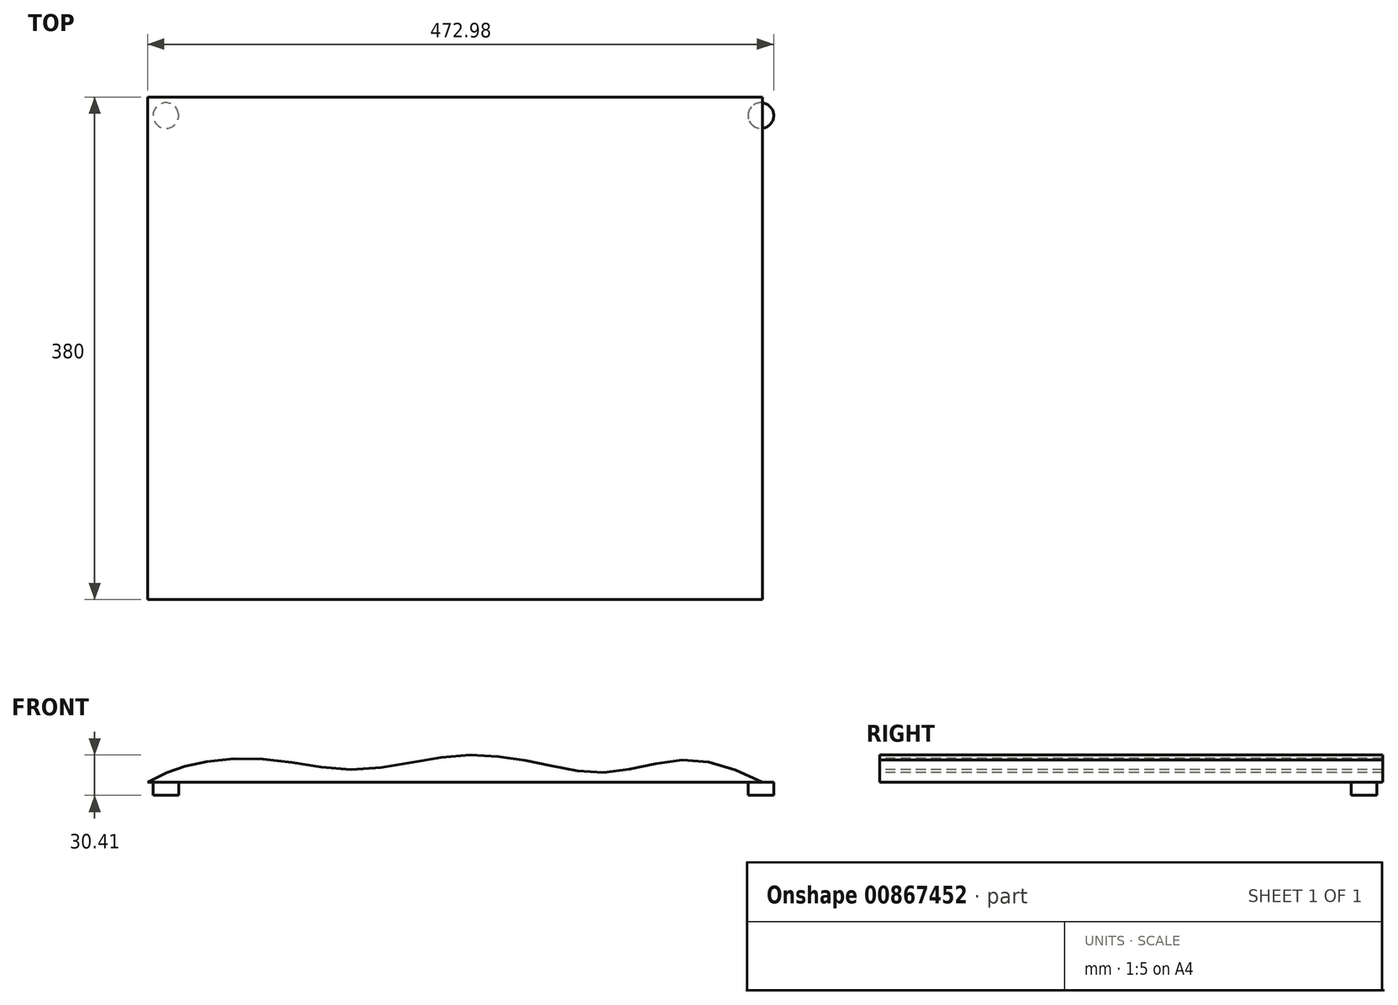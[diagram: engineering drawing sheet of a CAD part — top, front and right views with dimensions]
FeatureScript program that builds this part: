
annotation { "Feature Type Name" : "Feature", "Feature Type Description" : "" }
export const myFeature = defineFeature(function(context is Context, id is Id, definition is map)
    precondition{}
    {
        {
            var Q0;
            Q0=qCreatedBy(makeId("Front.planeOp"),FACE);
            var sketch = newSketch(context, id + "F0", { "sketchPlane" : qUnion([Q0])});
            skLineSegment(sketch, "E0", {"start": v(0, 0) * mm, "end": v(232.3, 0) * mm});
            skLineSegment(sketch, "E1", {"start": v(232.3, 0) * mm, "end": v(232.3, -47.02) * mm});
            skLineSegment(sketch, "E2.MirrorCS", {"start": v(464.59, 0) * mm, "end": v(232.3, 0) * mm});
            skFitSpline(sketch, "E3", {"points": [v(0, 0) * mm, v(30.55, 12.57) * mm, v(86.92, 17.52) * mm, v(157.37, 9.52) * mm, v(230.87, 19.8) * mm, v(292.57, 14.85) * mm, v(347.79, 7.44) * mm, v(404.1, 16.7) * mm, v(464.59, 0) * mm], "startDerivative": vector(394.31, 204.03) * mm, "endDerivative": vector(474.9, -243.15) * mm});
            skSolve(sketch);
        }
        {
            var Q0;
            Q0=makeQuery(id+"F0.imprint","IMPRINT",FACE,{"disambiguationData":[TD([[makeQuery(id+"F0.imprint","IMPRINT",EDGE,{"derivedFrom":sQuery(id+"F0.wireOp",EDGE,"E0")}),1.0]])]});
            extrude(context, id + "F1", {"entities" : qUnion([Q0]), "endBound" : BoundingType.SYMMETRIC, "depth" : 380 * mm, "offsetDistance" : 25 * mm});
        }
        {
            var Q0;
            Q0=qCreatedBy(makeId("Top.planeOp"),FACE);
            var sketch = newSketch(context, id + "F2", { "sketchPlane" : qUnion([Q0])});
            skCircle(sketch, "E4.MirrorC", {"center": v(13.76, 175.96) * mm, "radius": 9.68 * mm});
            skCircle(sketch, "E5.MirrorC", {"center": v(463.3, 175.96) * mm, "radius": 9.68 * mm});
            skSolve(sketch);
        }
        {
            var Q0;
            Q0 = qSketchRegion(id + "F2", true);
            extrude(context, id + "F3", {"entities" : qUnion([Q0]), "operationType" : NewBodyOperationType.ADD, "oppositeDirection" : true, "depth" : 10 * mm, "offsetDistance" : 25 * mm});
        }
    });
